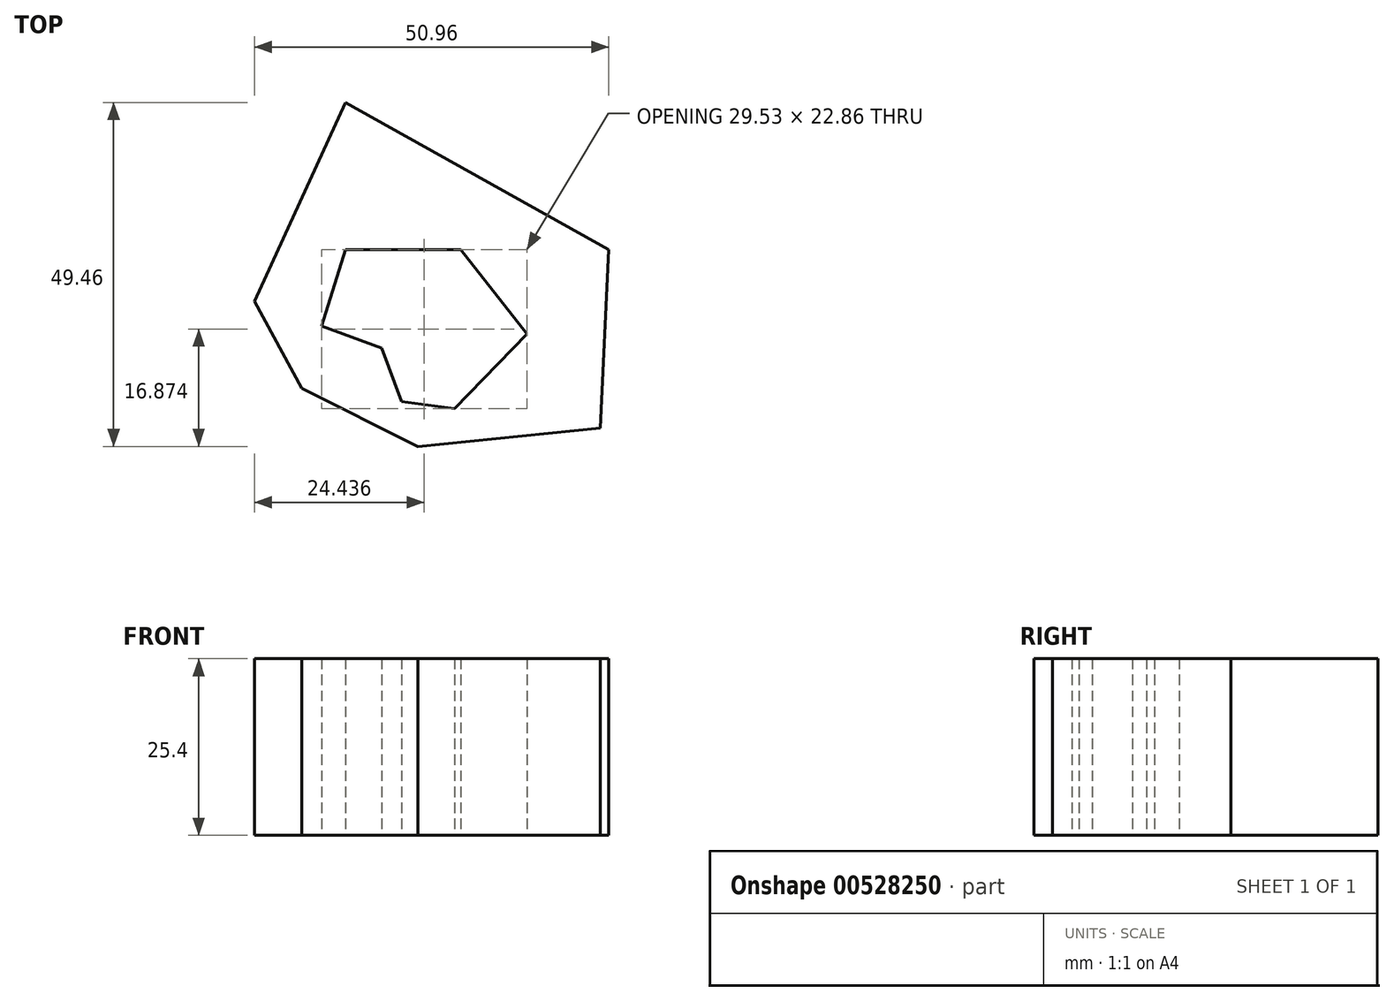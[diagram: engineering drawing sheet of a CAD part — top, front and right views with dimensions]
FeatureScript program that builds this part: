
annotation { "Feature Type Name" : "Feature", "Feature Type Description" : "" }
export const myFeature = defineFeature(function(context is Context, id is Id, definition is map)
    precondition{}
    {
        {
            var Q0;
            Q0=qCreatedBy(makeId("Top.planeOp"),FACE);
            var sketch = newSketch(context, id + "F0", { "sketchPlane" : qUnion([Q0])});
            skLineSegment(sketch, "E0", {"start": v(-49.47, 28.76) * mm, "end": v(-11.62, 28.76) * mm});
            skLineSegment(sketch, "E1", {"start": v(-12.81, 3.13) * mm, "end": v(-11.62, 28.76) * mm});
            skLineSegment(sketch, "E2", {"start": v(-12.81, 3.13) * mm, "end": v(-49.47, 28.76) * mm});
            skLineSegment(sketch, "E3", {"start": v(-55.72, 8.8) * mm, "end": v(-11.62, 28.76) * mm});
            skLineSegment(sketch, "E4", {"start": v(-49.47, 28.76) * mm, "end": v(-39.04, 0.45) * mm});
            skLineSegment(sketch, "E5", {"start": v(-39.04, 0.45) * mm, "end": v(-12.81, 3.13) * mm});
            skLineSegment(sketch, "E6", {"start": v(-55.72, 8.8) * mm, "end": v(-49.47, 28.76) * mm});
            skLineSegment(sketch, "E7", {"start": v(-55.72, 8.8) * mm, "end": v(-39.04, 0.45) * mm});
            skLineSegment(sketch, "E8", {"start": v(-39.04, 0.45) * mm, "end": v(-11.62, 28.76) * mm});
            skLineSegment(sketch, "E9", {"start": v(-12.81, 3.13) * mm, "end": v(-55.72, 8.8) * mm});
            skLineSegment(sketch, "E10", {"start": v(-62.58, 21.3) * mm, "end": v(-49.47, 49.91) * mm});
            skLineSegment(sketch, "E11", {"start": v(-49.47, 28.76) * mm, "end": v(-49.47, 49.91) * mm});
            skLineSegment(sketch, "E12", {"start": v(-49.47, 49.91) * mm, "end": v(-11.62, 28.76) * mm});
            skLineSegment(sketch, "E13", {"start": v(-49.47, 49.91) * mm, "end": v(-12.81, 3.13) * mm});
            skLineSegment(sketch, "E14", {"start": v(-62.58, 21.3) * mm, "end": v(-55.72, 8.8) * mm});
            skLineSegment(sketch, "E15", {"start": v(-49.47, 28.76) * mm, "end": v(-62.58, 21.3) * mm});
            skLineSegment(sketch, "E16", {"start": v(-62.58, 21.3) * mm, "end": v(-11.62, 28.76) * mm});
            skLineSegment(sketch, "E17", {"start": v(-12.81, 3.13) * mm, "end": v(-62.58, 21.3) * mm});
            skLineSegment(sketch, "E18", {"start": v(-49.47, 49.91) * mm, "end": v(-39.04, 0.45) * mm});
            skSolve(sketch);
        }
        {
            var Q0;
            Q0 = qSketchRegion(id + "F0", true);
            extrude(context, id + "F1", {"entities" : qUnion([Q0]), "depth" : 25.4 * mm, "offsetDistance" : 25.4 * mm});
        }
    });
